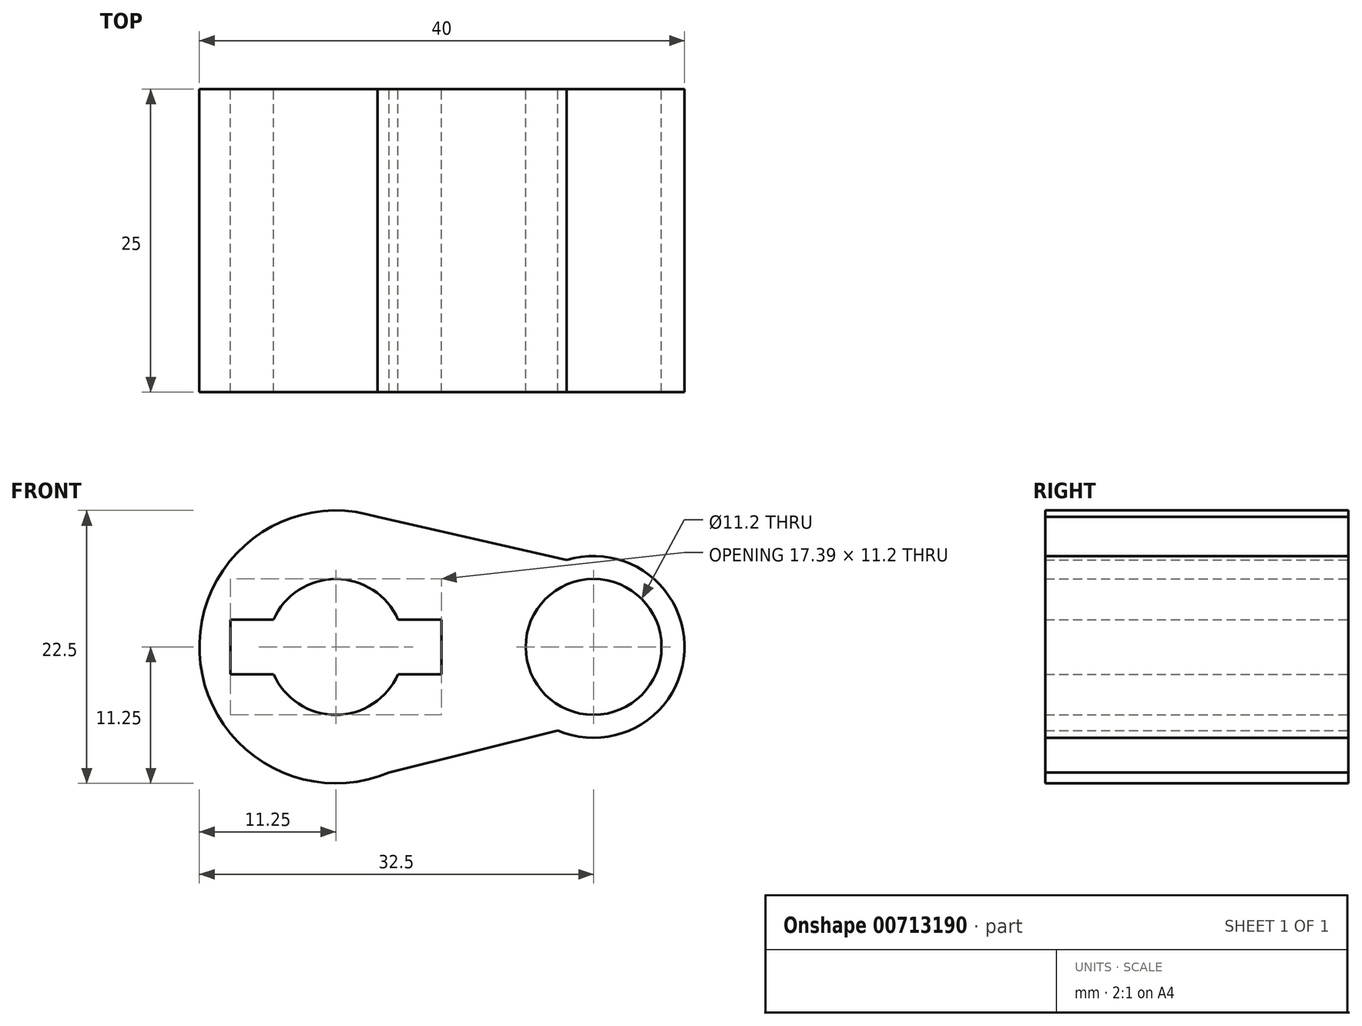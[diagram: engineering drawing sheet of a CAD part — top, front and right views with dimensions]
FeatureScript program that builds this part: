
annotation { "Feature Type Name" : "Feature", "Feature Type Description" : "" }
export const myFeature = defineFeature(function(context is Context, id is Id, definition is map)
    precondition{}
    {
        {
            var Q0;
            Q0=qCreatedBy(makeId("Front.planeOp"),FACE);
            var sketch = newSketch(context, id + "F0", { "sketchPlane" : qUnion([Q0])});
            skCircle(sketch, "E0", {"center": v(0, 0) * mm, "radius": 11.25 * mm});
            skCircle(sketch, "E1", {"center": v(21.25, 0) * mm, "radius": 7.5 * mm});
            skLineSegment(sketch, "E2", {"start": v(3.43, 10.72) * mm, "end": v(19.03, 7.16) * mm});
            skLineSegment(sketch, "E3", {"start": v(4.39, -10.36) * mm, "end": v(18.3, -6.9) * mm});
            skCircle(sketch, "E4", {"center": v(0, 0) * mm, "radius": 5.6 * mm});
            skCircle(sketch, "E5", {"center": v(21.25, 0) * mm, "radius": 5.6 * mm});
            skLineSegment(sketch, "E6.bottom", {"start": v(8.7, -2.25) * mm, "end": v(-8.7, -2.25) * mm});
            skLineSegment(sketch, "E6.top", {"start": v(8.7, 2.25) * mm, "end": v(-8.7, 2.25) * mm});
            skLineSegment(sketch, "E6.left", {"start": v(8.7, -2.25) * mm, "end": v(8.7, 2.25) * mm});
            skLineSegment(sketch, "E6.right", {"start": v(-8.7, -2.25) * mm, "end": v(-8.7, 2.25) * mm});
            skSolve(sketch);
        }
        {
            var Q0;
            {var subQ7=sQuery(id+"F0.wireOp",EDGE,"E6.left");Q0=makeQuery(id+"F0.imprint","IMPRINT",FACE,{"disambiguationData":[TD([[makeQuery(id+"F0.imprint","IMPRINT",EDGE,{"derivedFrom":subQ7}),-1.0]])]});}
            var Q1;
            {var subQ0=sQuery(id+"F0.wireOp",EDGE,"E2");Q1=makeQuery(id+"F0.imprint","IMPRINT",FACE,{"disambiguationData":[TD([[makeQuery(id+"F0.imprint","IMPRINT",EDGE,{"derivedFrom":subQ0}),-1.0]])]});}
            var Q2;
            Q2=makeQuery(id+"F0.imprint","IMPRINT",FACE,{"disambiguationData":[TD([[makeQuery(id+"F0.imprint","IMPRINT",EDGE,{"derivedFrom":sQuery(id+"F0.wireOp",EDGE,"E5")}),-1.0]])]});
            extrude(context, id + "F1", {"entities" : qUnion([Q0, Q1, Q2]), "depth" : 25 * mm, "offsetDistance" : 25 * mm});
        }
    });
